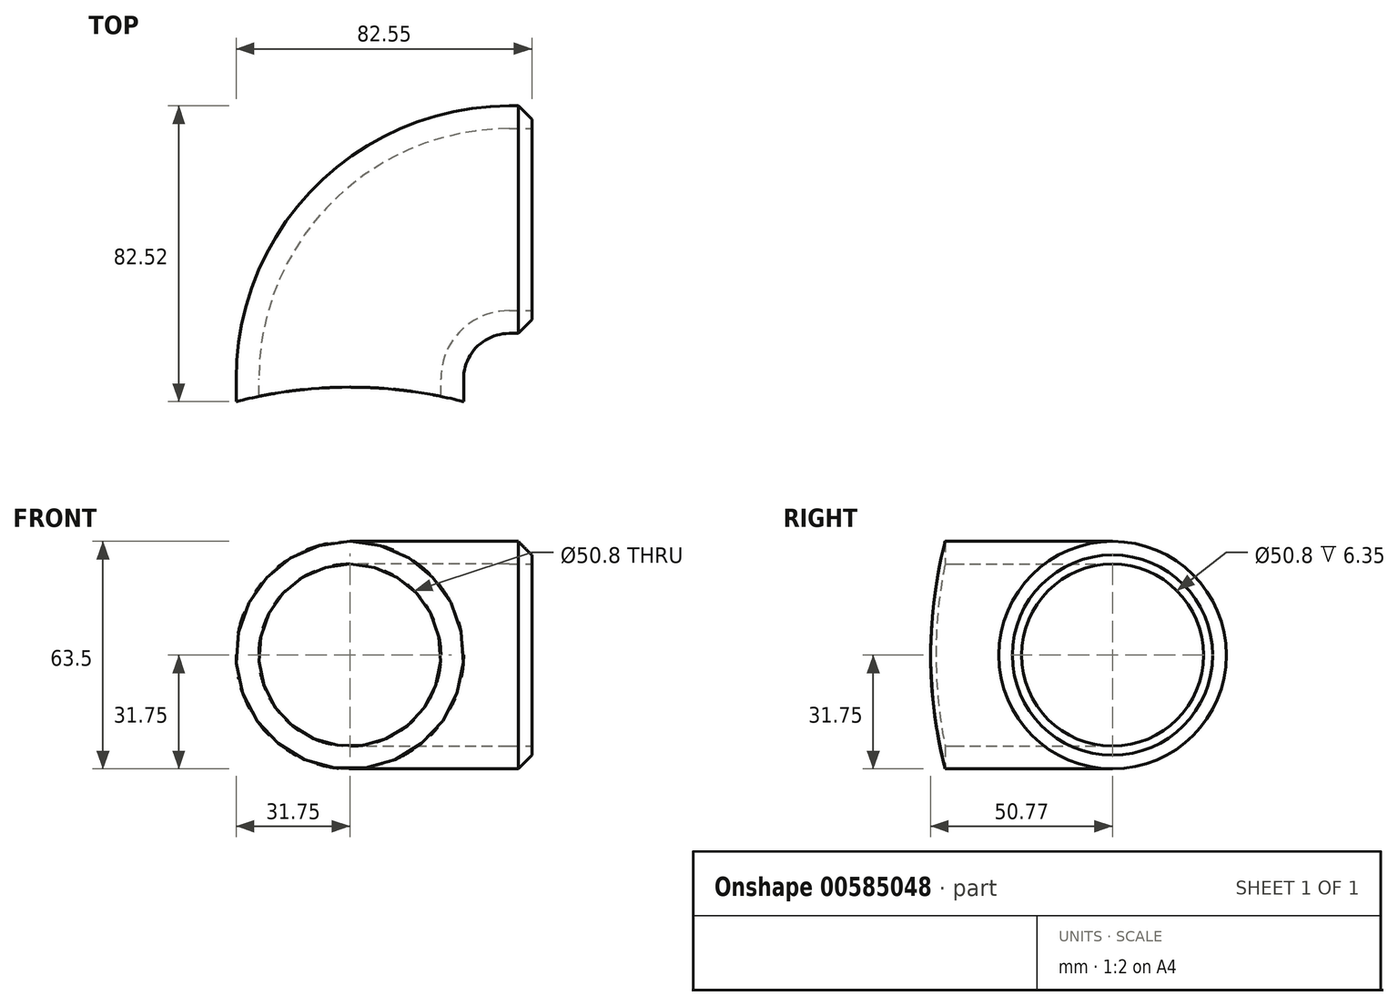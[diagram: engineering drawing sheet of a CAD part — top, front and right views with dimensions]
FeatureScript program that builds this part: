
annotation { "Feature Type Name" : "Feature", "Feature Type Description" : "" }
export const myFeature = defineFeature(function(context is Context, id is Id, definition is map)
    precondition{}
    {
        {
            var Q0;
            Q0=qCreatedBy(makeId("Top.planeOp"),FACE);
            var sketch = newSketch(context, id + "F0", { "sketchPlane" : qUnion([Q0])});
            skLineSegment(sketch, "E0", {"start": v(0, 0) * mm, "end": v(0, 6.35) * mm});
            skLineSegment(sketch, "E1", {"start": v(44.45, 50.8) * mm, "end": v(50.8, 50.8) * mm});
            skArc(sketch, "E2", {"start": v(44.45, 50.8) * mm, "mid": v(13.02, 37.78) * mm, "end": v(0, 6.35) * mm});
            skPoint(sketch, "E3.orphan", {"position": v(0, 50.8) * mm});
            skSolve(sketch);
        }
        {
            var Q0;
            Q0=qCreatedBy(makeId("Front.planeOp"),FACE);
            var sketch = newSketch(context, id + "F1", { "sketchPlane" : qUnion([Q0])});
            skCircle(sketch, "E4", {"center": v(0, 0) * mm, "radius": 31.75 * mm});
            skCircle(sketch, "E5.0", {"center": v(0, 0) * mm, "radius": 25.4 * mm});
            skSolve(sketch);
        }
        {
            var Q0;
            Q0=makeQuery(id+"F1.imprint","IMPRINT",FACE,{"disambiguationData":[TD([[makeQuery(id+"F1.imprint","IMPRINT",EDGE,{"derivedFrom":sQuery(id+"F1.wireOp",EDGE,"E4")}),1.0]])]});
            var Q1;
            Q1 = qConstructionFilter(qBodyType(qCreatedBy(id + "F0" ,EDGE), BodyType.WIRE), ConstructionObject.NO);
            sweep(context, id + "F2", {"profiles" : qUnion([Q0]), "path" : qUnion([Q1])});
        }
        {
            var Q0;
            Q0=qCreatedBy(makeId("Top.planeOp"),FACE);
            var sketch = newSketch(context, id + "F3", { "sketchPlane" : qUnion([Q0])});
            skCircle(sketch, "E6", {"center": v(0, -122.94) * mm, "radius": 127 * mm});
            skSolve(sketch);
        }
        {
            var Q0;
            Q0 = qSketchRegion(id + "F3", true);
            extrude(context, id + "F4", {"entities" : qUnion([Q0]), "operationType" : NewBodyOperationType.REMOVE, "depth" : 101.6 * mm, "offsetDistance" : 25.4 * mm, "symmetric" : true});
        }
        {
            var Q0;
            Q0=makeQuery(id+"F2.opSweep","CAP_EDGE",EDGE,{"disambiguationData":[OSD([sQuery(id+"F0.wireOp",VERTEX,"E1.end"),sQuery(id+"F1.wireOp",EDGE,"E4")])],"isStart":false});
            chamfer(context, id + "F5", {"entities" : qUnion([Q0]), "width" : 3.8 * mm, "tangentPropagation" : true});
        }
    });
